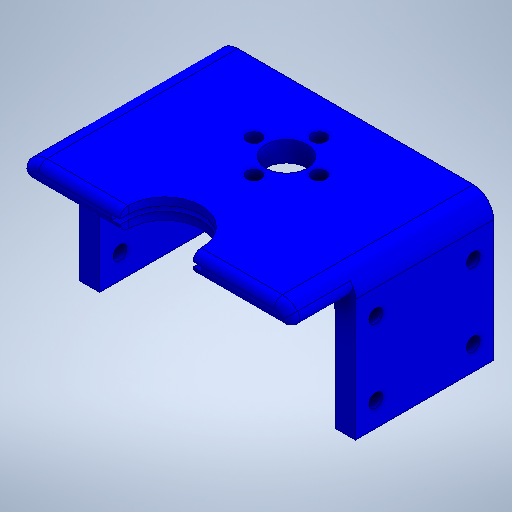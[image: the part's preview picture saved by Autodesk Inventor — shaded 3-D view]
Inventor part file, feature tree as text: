
AUTODESK INVENTOR PART (.ipt)
format: ipt  version: 2025.2 (Build 292293000, 293)  size: 359,424 bytes
history: native  units: mm
features: sketch x7, extrude x5, fillet x3, hole x1
ambient origin geometry x8: Origin, YZ Plane, XZ Plane, XY Plane, X Axis, Y Axis, Z Axis, Center Point
bodies: Solid1 (feature_tree)
feature tree (16):
  extrude  "Extrusion1"  Depth=34.0mm
  extrude  "Extrusion2"  Depth=16.0mm
  hole  "Hole1"  [1 undecoded]
  fillet  "Fillet1"  Radius=5.0mm
  extrude  "Extrusion3"  Depth=5.0mm
  fillet  "Fillet2"  Radius=30.0mm
  fillet  "Fillet3"  Radius=5.0mm
  extrude  "Extrusion4"  Depth=5.0mm
  extrude  "Extrusion5"  Depth=5.0mm
  sketch  "Sketch1"  dims[d0=68.0mm d1=34.0mm]
  sketch  "Sketch Circular Pattern1"  dims[d2=10.2mm d3=16.0mm]
  sketch  "Sketch2"  dims[d4=3.5mm d5=40.0mm d7=360.0deg d9=5.0mm d10=0.0mm]
  sketch  "Sketch3"  dims[d11=5.0mm d12=5.0mm d13=30.0mm d14=0.0mm d15=5.0mm]
  sketch  "Sketch4"  dims[d16=5.0mm d17=6.0mm]
  sketch  "Sketch5"  dims[d18=6.0mm]
  sketch  "Sketch6"  dims[d19=3.4mm d20=6.0mm d21=4.0mm d22=2.0mm d23=90.0deg d24=8.0mm d25=20.594885mm d26=5.0mm d27=15.0mm d28=0.0mm d29=5.0mm d30=2.0mm d31=21.0mm d32=2.0mm d33=18.0mm d34=3.1mm d35=0.0mm d36=22.0mm d37=1.2mm d38=15.0mm d39=0.0mm d40=0.5mm d41=0.872665mm d42=0.5mm d43=0.872665mm]
note: 1 required parameter value undecoded (feature->parameter linkage not recoverable at this tier; creation-order binding heuristic only, values carry confidence <= 0.55)
